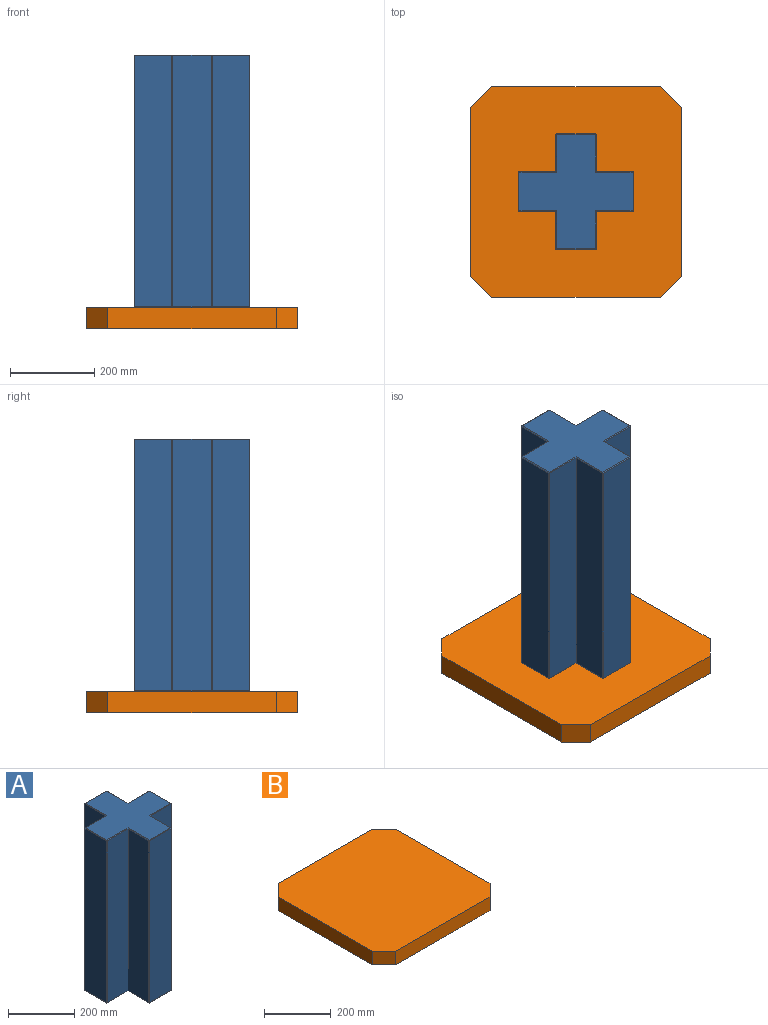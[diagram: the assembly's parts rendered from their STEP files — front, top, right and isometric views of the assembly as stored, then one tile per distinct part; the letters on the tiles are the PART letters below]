
ASSEMBLY  parts=2 mates=1
PART A: 62 faces, bbox 275x275x600 mm
  f0: plane 596x91mm, normal (1,0,0), area 54236mm2, adj f26,f31,f35,f36
  f1: plane 596x88mm, normal (0,1,0), area 52448mm2, adj f2,f36,f41,f45
  f2: plane 596x88mm, normal (1,0,0), area 52448mm2, adj f1,f46,f49,f50
  f3: plane 596x91mm, normal (0,1,0), area 54236mm2, adj f50,f55,f58,f61
  f4: plane 596x88mm, normal (-1,0,0), area 52448mm2, adj f5,f56,f57,f61
  f5: plane 596x88mm, normal (0,1,0), area 52448mm2, adj f4,f43,f52,f53
  f6: plane 596x91mm, normal (-1,0,0), area 54236mm2, adj f33,f42,f43,f44
  f7: plane 596x88mm, normal (0,-1,0), area 52448mm2, adj f8,f32,f33,f34
  f8: plane 596x88mm, normal (-1,0,0), area 52448mm2, adj f7,f19,f28,f29
  f9: plane 596x91mm, normal (0,-1,0), area 54236mm2, adj f14,f18,f19,f20
  f10: plane 596x88mm, normal (1,0,0), area 52448mm2, adj f11,f14,f17,f21
  f11: plane 596x88mm, normal (0,-1,0), area 52448mm2, adj f10,f22,f25,f26
  f12: plane 271x271mm, normal (0,0,1), area 41041mm2, adj f17,f18,f22,f28,f31,f32,f41,f42
  f13: plane 271x271mm, normal (0,0,-1), area 41041mm2, adj f20,f21,f25,f29,f34,f35,f44,f45
  f14: plane 596x2mm, normal (0.71,-0.71,0), area 1685.7mm2, adj f9,f10,f15,f16
  f15: plane 2x2mm, normal (0.58,-0.58,0.58), area 3.5mm2, adj f14,f17,f18
  f16: plane 2x2mm, normal (0.58,-0.58,-0.58), area 3.5mm2, adj f14,f20,f21
  f17: plane 90x2mm, normal (0.71,0,0.71), area 251.7mm2, adj f10,f12,f15,f22
  f18: plane 91x2mm, normal (0,-0.71,0.71), area 257.4mm2, adj f9,f12,f15,f23
  f19: plane 596x2mm, normal (-0.71,-0.71,0), area 1685.7mm2, adj f8,f9,f23,f24
  f20: plane 91x2mm, normal (0,-0.71,-0.71), area 257.4mm2, adj f9,f13,f16,f24
  f21: plane 90x2mm, normal (0.71,0,-0.71), area 251.7mm2, adj f10,f13,f16,f25
  f22: plane 90x2mm, normal (0,-0.71,0.71), area 251.7mm2, adj f11,f12,f17,f27
  f23: plane 2x2mm, normal (-0.58,-0.58,0.58), area 3.5mm2, adj f18,f19,f28
  f24: plane 2x2mm, normal (-0.58,-0.58,-0.58), area 3.5mm2, adj f19,f20,f29
  f25: plane 90x2mm, normal (0,-0.71,-0.71), area 251.7mm2, adj f11,f13,f21,f30
  f26: plane 596x2mm, normal (0.71,-0.71,0), area 1685.7mm2, adj f0,f11,f27,f30
  f27: plane 2x2mm, normal (0.58,-0.58,0.58), area 3.5mm2, adj f22,f26,f31
  f28: plane 90x2mm, normal (-0.71,0,0.71), area 251.7mm2, adj f8,f12,f23,f32
  f29: plane 90x2mm, normal (-0.71,0,-0.71), area 251.7mm2, adj f8,f13,f24,f34
  f30: plane 2x2mm, normal (0.58,-0.58,-0.58), area 3.5mm2, adj f25,f26,f35
  f31: plane 91x2mm, normal (0.71,0,0.71), area 257.4mm2, adj f0,f12,f27,f37
  f32: plane 90x2mm, normal (0,-0.71,0.71), area 251.7mm2, adj f7,f12,f28,f38
  f33: plane 596x2mm, normal (-0.71,-0.71,0), area 1685.7mm2, adj f6,f7,f38,f39
  f34: plane 90x2mm, normal (0,-0.71,-0.71), area 251.7mm2, adj f7,f13,f29,f39
  f35: plane 91x2mm, normal (0.71,0,-0.71), area 257.4mm2, adj f0,f13,f30,f40
  f36: plane 596x2mm, normal (0.71,0.71,0), area 1685.7mm2, adj f0,f1,f37,f40
  f37: plane 2x2mm, normal (0.58,0.58,0.58), area 3.5mm2, adj f31,f36,f41
  f38: plane 2x2mm, normal (-0.58,-0.58,0.58), area 3.5mm2, adj f32,f33,f42
  f39: plane 2x2mm, normal (-0.58,-0.58,-0.58), area 3.5mm2, adj f33,f34,f44
  f40: plane 2x2mm, normal (0.58,0.58,-0.58), area 3.5mm2, adj f35,f36,f45
  f41: plane 90x2mm, normal (0,0.71,0.71), area 251.7mm2, adj f1,f12,f37,f46
  f42: plane 91x2mm, normal (-0.71,0,0.71), area 257.4mm2, adj f6,f12,f38,f47
  f43: plane 596x2mm, normal (-0.71,0.71,0), area 1685.7mm2, adj f5,f6,f47,f48
  f44: plane 91x2mm, normal (-0.71,0,-0.71), area 257.4mm2, adj f6,f13,f39,f48
  f45: plane 90x2mm, normal (0,0.71,-0.71), area 251.7mm2, adj f1,f13,f40,f49
  f46: plane 90x2mm, normal (0.71,0,0.71), area 251.7mm2, adj f2,f12,f41,f51
  f47: plane 2x2mm, normal (-0.58,0.58,0.58), area 3.5mm2, adj f42,f43,f52
  f48: plane 2x2mm, normal (-0.58,0.58,-0.58), area 3.5mm2, adj f43,f44,f53
  f49: plane 90x2mm, normal (0.71,0,-0.71), area 251.7mm2, adj f2,f13,f45,f54
  f50: plane 596x2mm, normal (0.71,0.71,0), area 1685.7mm2, adj f2,f3,f51,f54
  f51: plane 2x2mm, normal (0.58,0.58,0.58), area 3.5mm2, adj f46,f50,f55
  f52: plane 90x2mm, normal (0,0.71,0.71), area 251.7mm2, adj f5,f12,f47,f56
  f53: plane 90x2mm, normal (0,0.71,-0.71), area 251.7mm2, adj f5,f13,f48,f57
  f54: plane 2x2mm, normal (0.58,0.58,-0.58), area 3.5mm2, adj f49,f50,f58
  f55: plane 91x2mm, normal (0,0.71,0.71), area 257.4mm2, adj f3,f12,f51,f59
  f56: plane 90x2mm, normal (-0.71,0,0.71), area 251.7mm2, adj f4,f12,f52,f59
  f57: plane 90x2mm, normal (-0.71,0,-0.71), area 251.7mm2, adj f4,f13,f53,f60
  f58: plane 91x2mm, normal (0,0.71,-0.71), area 257.4mm2, adj f3,f13,f54,f60
  f59: plane 2x2mm, normal (-0.58,0.58,0.58), area 3.5mm2, adj f55,f56,f61
  f60: plane 2x2mm, normal (-0.58,0.58,-0.58), area 3.5mm2, adj f57,f58,f61
  f61: plane 596x2mm, normal (-0.71,0.71,0), area 1685.7mm2, adj f3,f4,f59,f60
PART B: 10 faces, bbox 500x500x50 mm
  f0: plane 50x50mm, normal (0.71,0.71,0), area 3535.5mm2, adj f1,f7,f8,f9
  f1: plane 400x50mm, normal (0,1,0), area 20000mm2, adj f0,f2,f8,f9
  f2: plane 50x50mm, normal (-0.71,0.71,0), area 3535.5mm2, adj f1,f3,f8,f9
  f3: plane 400x50mm, normal (-1,0,0), area 20000mm2, adj f2,f4,f8,f9
  f4: plane 50x50mm, normal (-0.71,-0.71,0), area 3535.5mm2, adj f3,f5,f8,f9
  f5: plane 400x50mm, normal (0,-1,0), area 20000mm2, adj f4,f6,f8,f9
  f6: plane 50x50mm, normal (0.71,-0.71,0), area 3535.5mm2, adj f5,f7,f8,f9
  f7: plane 400x50mm, normal (1,0,0), area 20000mm2, adj f0,f6,f8,f9
  f8: plane 500x500mm, normal (0,0,1), area 245000mm2, adj f0,f1,f2,f3,f4,f5,f6,f7
  f9: plane 500x500mm, normal (0,0,-1), area 245000mm2, adj f0,f1,f2,f3,f4,f5,f6,f7
PLACE A t=(0,0,50)mm
PLACE B at identity
MATE fastened B.f8 <-> A.f13  axis (0,0,1) through (0,0,50)mm
